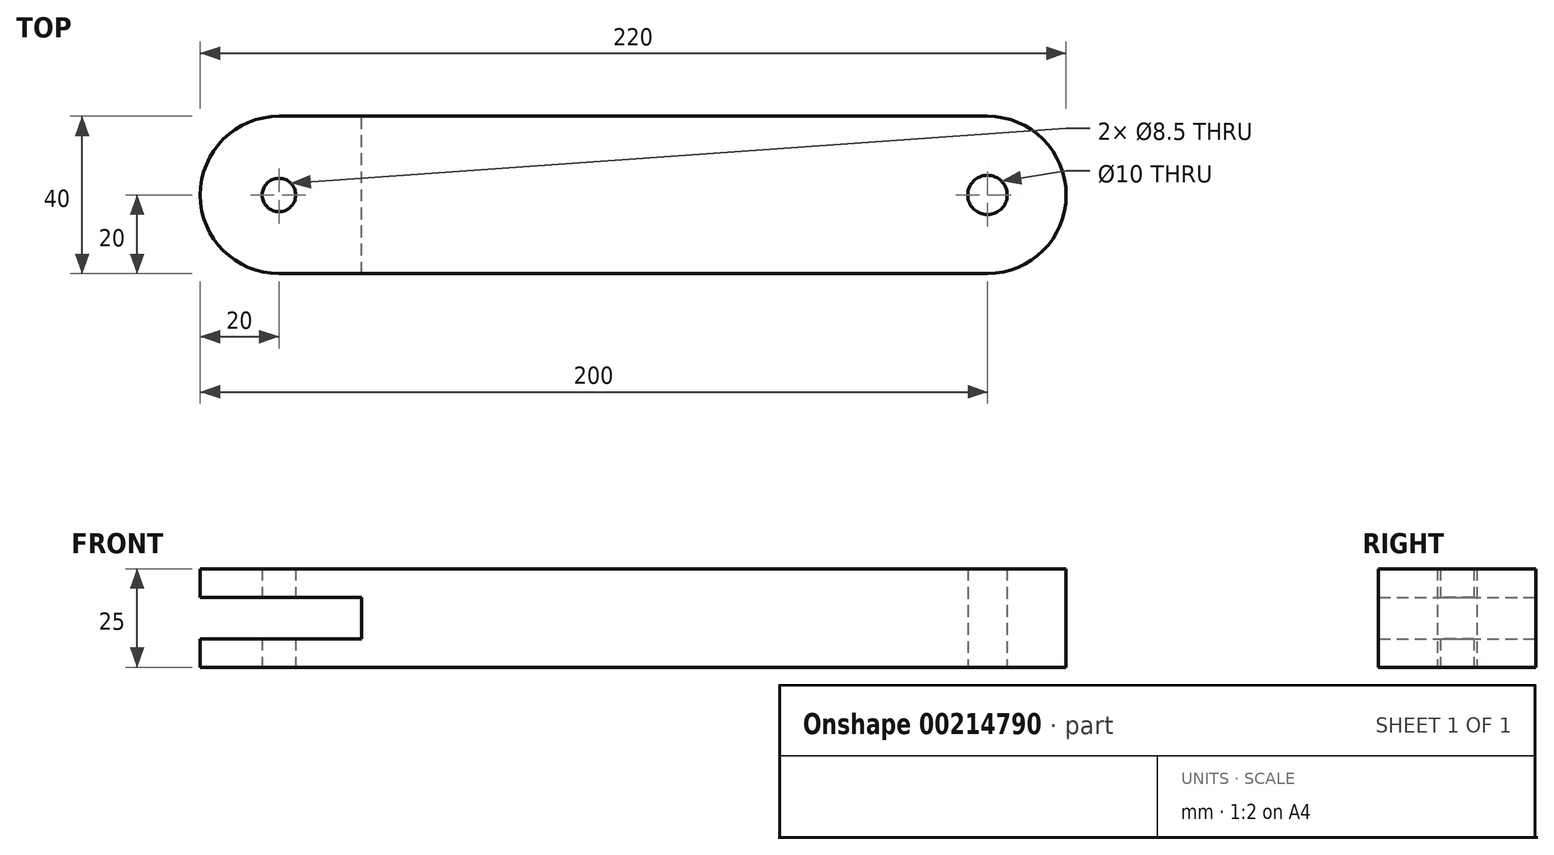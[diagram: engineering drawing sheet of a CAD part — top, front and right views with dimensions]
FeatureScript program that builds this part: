
annotation { "Feature Type Name" : "Feature", "Feature Type Description" : "" }
export const myFeature = defineFeature(function(context is Context, id is Id, definition is map)
    precondition{}
    {
        {
            var Q0;
            Q0=qCreatedBy(makeId("Top.planeOp"),FACE);
            var sketch = newSketch(context, id + "F0", { "sketchPlane" : qUnion([Q0])});
            skLineSegment(sketch, "E0.bottom", {"start": v(110, 20) * mm, "end": v(-110, 20) * mm});
            skLineSegment(sketch, "E0.top", {"start": v(110, -20) * mm, "end": v(-110, -20) * mm});
            skLineSegment(sketch, "E0.left", {"start": v(110, 20) * mm, "end": v(110, -20) * mm});
            skLineSegment(sketch, "E0.right", {"start": v(-110, 20) * mm, "end": v(-110, -20) * mm});
            skPoint(sketch, "E0.middle", {"position": v(0, 0) * mm});
            skSolve(sketch);
        }
        {
            var Q0;
            Q0=makeQuery(id+"F0.imprint","IMPRINT",FACE,{"disambiguationData":[TD([[makeQuery(id+"F0.imprint","IMPRINT",EDGE,{"derivedFrom":sQuery(id+"F0.wireOp",EDGE,"E0.bottom")}),1.0]])]});
            extrude(context, id + "F1", {"entities" : qUnion([Q0]), "endBound" : BoundingType.SYMMETRIC, "depth" : 25 * mm});
        }
        {
            var Q0;
            Q0=qCreatedBy(makeId("Front.planeOp"),FACE);
            var sketch = newSketch(context, id + "F2", { "sketchPlane" : qUnion([Q0])});
            skLineSegment(sketch, "E1.bottom", {"start": v(-110, 0) * mm, "end": v(-110, 0) * mm});
            skLineSegment(sketch, "E1.top", {"start": v(-110, 0) * mm, "end": v(-110, 0) * mm});
            skLineSegment(sketch, "E1.left", {"start": v(-110, 0) * mm, "end": v(-110, 0) * mm});
            skLineSegment(sketch, "E1.right", {"start": v(-110, 0) * mm, "end": v(-110, 0) * mm});
            skPoint(sketch, "E1.middle", {"position": v(-110, 0) * mm});
            skLineSegment(sketch, "E2.bottom", {"start": v(-69, -5.25) * mm, "end": v(-110, -5.25) * mm});
            skLineSegment(sketch, "E2.top", {"start": v(-69, 5.25) * mm, "end": v(-110, 5.25) * mm});
            skLineSegment(sketch, "E2.left", {"start": v(-69, -5.25) * mm, "end": v(-69, 5.25) * mm});
            skLineSegment(sketch, "E2.right", {"start": v(-110, -5.25) * mm, "end": v(-110, 5.25) * mm});
            skPoint(sketch, "E2.middle", {"position": v(-89.5, 0) * mm});
            skSolve(sketch);
        }
        {
            var Q0;
            Q0=makeQuery(id+"F2.imprint","IMPRINT",FACE,{"disambiguationData":[TD([[makeQuery(id+"F2.imprint","IMPRINT",EDGE,{"derivedFrom":sQuery(id+"F2.wireOp",EDGE,"E2.bottom")}),-1.0]])]});
            extrude(context, id + "F3", {"entities" : qUnion([Q0]), "operationType" : NewBodyOperationType.REMOVE, "endBound" : BoundingType.SYMMETRIC, "depth" : 40 * mm});
        }
        {
            var Q0;
            {var subQ0=sQuery(id+"F0.wireOp",EDGE,"E0.bottom");var subQ1=sQuery(id+"F0.wireOp",EDGE,"E0.right");Q0=makeQuery(id+"F3.boolean.opBoolean","SPLIT",EDGE,{"disambiguationData":[TD([makeQuery(id+"F3.opExtrude","SWEPT_FACE",FACE,{"disambiguationData":[OSD([sQuery(id+"F2.wireOp",EDGE,"E2.top")])]})])],"derivedFrom":makeQuery(id+"F1.opExtrude","SWEPT_EDGE",EDGE,{"disambiguationData":[OSD([subQ0,subQ1])]})});}
            var Q1;
            {var subQ0=sQuery(id+"F0.wireOp",EDGE,"E0.right");var subQ1=sQuery(id+"F0.wireOp",EDGE,"E0.top");Q1=makeQuery(id+"F3.boolean.opBoolean","SPLIT",EDGE,{"disambiguationData":[TD([makeQuery(id+"F3.opExtrude","SWEPT_FACE",FACE,{"disambiguationData":[OSD([sQuery(id+"F2.wireOp",EDGE,"E2.top")])]})])],"derivedFrom":makeQuery(id+"F1.opExtrude","SWEPT_EDGE",EDGE,{"disambiguationData":[OSD([subQ1,subQ0])]})});}
            var Q2;
            {var subQ0=sQuery(id+"F0.wireOp",EDGE,"E0.right");var subQ1=sQuery(id+"F0.wireOp",EDGE,"E0.top");Q2=makeQuery(id+"F3.boolean.opBoolean","SPLIT",EDGE,{"disambiguationData":[TD([makeQuery(id+"F3.opExtrude","SWEPT_FACE",FACE,{"disambiguationData":[OSD([sQuery(id+"F2.wireOp",EDGE,"E2.bottom")])]})])],"derivedFrom":makeQuery(id+"F1.opExtrude","SWEPT_EDGE",EDGE,{"disambiguationData":[OSD([subQ1,subQ0])]})});}
            var Q3;
            {var subQ0=sQuery(id+"F0.wireOp",EDGE,"E0.bottom");var subQ1=sQuery(id+"F0.wireOp",EDGE,"E0.right");Q3=makeQuery(id+"F3.boolean.opBoolean","SPLIT",EDGE,{"disambiguationData":[TD([makeQuery(id+"F3.opExtrude","SWEPT_FACE",FACE,{"disambiguationData":[OSD([sQuery(id+"F2.wireOp",EDGE,"E2.bottom")])]})])],"derivedFrom":makeQuery(id+"F1.opExtrude","SWEPT_EDGE",EDGE,{"disambiguationData":[OSD([subQ0,subQ1])]})});}
            fillet(context, id + "F4", {"entities" : qUnion([Q0, Q1, Q2, Q3]), "radius" : 20 * mm, "tangentPropagation" : true, "allowEdgeOverflow" : false});
        }
        {
            var Q0;
            Q0=makeQuery(id+"F1.opExtrude","CAP_FACE",FACE,{"disambiguationData":[OSD([sQuery(id+"F0.wireOp",EDGE,"E0.bottom"),sQuery(id+"F0.wireOp",EDGE,"E0.top"),sQuery(id+"F0.wireOp",EDGE,"E0.left"),sQuery(id+"F0.wireOp",EDGE,"E0.right")])],"isStart":true});
            var sketch = newSketch(context, id + "F5", { "sketchPlane" : qUnion([Q0])});
            skPoint(sketch, "E3", {"position": v(90, 0) * mm});
            skPoint(sketch, "E4", {"position": v(-90, 0) * mm});
            skSolve(sketch);
        }
        {
            var Q0;
            Q0=sQuery(id+"F5.wireOp",VERTEX,"E4");
            var Q1;
            Q1=makeQuery(id+"F1.opExtrude","SWEPT_BODY",BODY,{"disambiguationData":[OSD([sQuery(id+"F0.wireOp",EDGE,"E0.bottom"),sQuery(id+"F0.wireOp",EDGE,"E0.top"),sQuery(id+"F0.wireOp",EDGE,"E0.left"),sQuery(id+"F0.wireOp",EDGE,"E0.right")])]});
            hole(context, id + "F6", {"style" : HoleStyle.SIMPLE, "endStyle" : HoleEndStyle.THROUGH, "holeDiameter" : 8.5 * mm, "locations" : qUnion([Q0]), "scope" : qUnion([Q1]), "isTappedThrough" : true});
        }
        {
            var Q0;
            Q0=makeQuery(id+"F1.opExtrude","CAP_FACE",FACE,{"disambiguationData":[OSD([sQuery(id+"F0.wireOp",EDGE,"E0.bottom"),sQuery(id+"F0.wireOp",EDGE,"E0.top"),sQuery(id+"F0.wireOp",EDGE,"E0.left"),sQuery(id+"F0.wireOp",EDGE,"E0.right")])],"isStart":true});
            var sketch = newSketch(context, id + "F7", { "sketchPlane" : qUnion([Q0])});
            skPoint(sketch, "E5", {"position": v(90, 0) * mm});
            skCircle(sketch, "E6", {"center": v(90, 0) * mm, "radius": 13 * mm});
            skSolve(sketch);
        }
        {
            var Q0;
            Q0=sQuery(id+"F7.wireOp",VERTEX,"E5");
            var Q1;
            Q1=makeQuery(id+"F1.opExtrude","SWEPT_BODY",BODY,{"disambiguationData":[OSD([sQuery(id+"F0.wireOp",EDGE,"E0.bottom"),sQuery(id+"F0.wireOp",EDGE,"E0.top"),sQuery(id+"F0.wireOp",EDGE,"E0.left"),sQuery(id+"F0.wireOp",EDGE,"E0.right")])]});
            hole(context, id + "F8", {"style" : HoleStyle.SIMPLE, "endStyle" : HoleEndStyle.THROUGH, "holeDiameter" : 10 * mm, "locations" : qUnion([Q0]), "scope" : qUnion([Q1]), "isTappedThrough" : true});
        }
        {
            var Q0;
            Q0=makeQuery(id+"F1.opExtrude","SWEPT_EDGE",EDGE,{"disambiguationData":[OSD([sQuery(id+"F0.wireOp",EDGE,"E0.top"),sQuery(id+"F0.wireOp",EDGE,"E0.left")])]});
            var Q1;
            Q1=makeQuery(id+"F1.opExtrude","SWEPT_EDGE",EDGE,{"disambiguationData":[OSD([sQuery(id+"F0.wireOp",EDGE,"E0.bottom"),sQuery(id+"F0.wireOp",EDGE,"E0.left")])]});
            fillet(context, id + "F9", {"entities" : qUnion([Q0, Q1]), "radius" : 20 * mm, "tangentPropagation" : true, "allowEdgeOverflow" : false});
        }
    });
